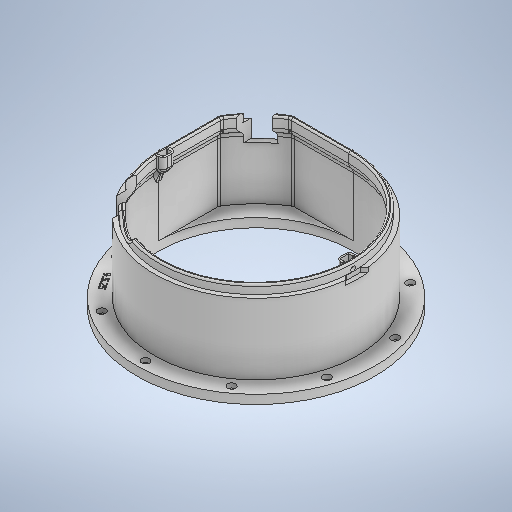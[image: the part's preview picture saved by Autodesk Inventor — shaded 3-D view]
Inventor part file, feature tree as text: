
AUTODESK INVENTOR PART (.ipt)
format: ipt  version: 2025 (Build 290162000, 162)  size: 1,504,256 bytes
history: native  units: mm
features: sketch x15, extrude x10, fillet x5, chamfer x3, hole x2, mirror x2, other x2, pattern_circular x1, plane x1
ambient origin geometry x8: Origin, YZ Plane, XZ Plane, XY Plane, X Axis, Y Axis, Z Axis, Center Point
bodies: Solid1 (feature_tree), Body (feature_tree)
feature tree (41):
  extrude  "Base"  Depth=10.0mm TaperAngle=0.0deg
  extrude  "Walls"  Depth=230.0mm
  extrude  "Overhang for Lip"  Depth=5.0mm TaperAngle=0.0deg
  fillet  "Fillet1"  Radius=5.0mm
  chamfer  "Chamfer1"  Distance=4.99mm Angle=45.0deg
  fillet  "Fillet2"  Radius=8.0mm
  extrude  "Lip"  Depth=5.0mm TaperAngle=0.0deg
  extrude  "8020 Beam Slot"  Depth=30.0mm
  extrude  "LV Window"  Depth=42.0mm
  fillet  "Fillet4"  Radius=53.266mm
  hole  "Hole1"  [1 undecoded]
  pattern_circular  "Circular Pattern1"  Count=10 Angle=360.0deg
  extrude  "Lock Tab Seats"  Depth=5.0mm TaperAngle=0.0deg
  mirror  "Mirror1"
  extrude  "Fill Extra Hole in Base"  Depth=7.0mm
  other  "LABEL"
  other  "DATE"
  plane  "Work Plane2"
  extrude  "Nut & Washer Seat"  Depth=1.0mm TaperAngle=0.0deg
  hole  "Hole2"  [1 undecoded]
  extrude  "Extrusion15"  Depth=5.0mm
  chamfer  "Chamfer2"  Distance=10.0mm
  fillet  "Fillet5"  Radius=17.0mm
  chamfer  "Chamfer3"  Distance=10.0mm
  mirror  "Mirror2"
  fillet  "Fillet7"  Radius=2.0mm
  sketch  "Sketch1"  dims[d1=270.0mm d2=10.0mm d3=0.0mm]
  sketch  "Sketch4"  dims[d15=220.0mm d16=230.0mm]
  sketch  "Sketch7"  dims[d17=80.0mm d18=0.0mm d24=5.0mm d25=0.0mm d26=5.0mm]
  sketch  "Sketch8"  dims[d27=5.0mm d28=4.99mm d29=2.0mm d30=45.0deg d31=8.0mm]
  sketch  "Sketch9"  dims[d32=5.0mm d33=10.0mm d34=0.0mm]
  sketch  "Sketch10"  dims[d36=20.0mm d37=30.0mm]
  sketch  "Sketch11"  dims[d39=0.0mm d40=0.0mm d41=42.0mm d42=53.266mm]
  sketch  "Sketch12"  dims[d43=22.0mm d44=0.0mm d45=0.0mm]
  sketch  "Sketch13"  dims[d46=2.0mm]
  sketch  "Sketch15"  dims[d47=5.5mm d48=6.0mm d49=9.0mm d50=5.0mm d51=90.0deg d52=8.0mm d53=20.594885mm]
  sketch  "Sketch16"  dims[d54=125.0mm d55=100.0mm d56=360.0deg]
  sketch  "Sketch18"  dims[d58=5.0mm d59=0.0mm d60=10.0mm d61=0.0mm]
  sketch  "Sketch19"  dims[d62=8.0mm d63=7.0mm]
  sketch  "Sketch20"  dims[d64=32.0mm d67=1.0mm d68=0.0mm]
  sketch  "Sketch21"  dims[d69=1.0mm d70=0.0mm d71=-118.0mm d76=15.4mm d77=10.0mm d78=17.0mm d79=0.0mm d80=10.0mm d81=2.0mm d82=5.15mm d83=1.6mm d84=5.15mm d85=12.0mm d86=12.7mm d87=0.0mm d88=5.5mm d89=6.0mm d90=4.0mm d91=2.0mm d92=90.0deg d93=8.0mm d94=20.594885mm d95=7.5mm d96=0.8mm d97=0.0mm d98=0.5mm d99=2.0mm d100=45.0deg d101=15.0mm d102=3.5mm d103=2.0mm d104=45.0deg d106=5.0mm d109=88.16mm]
note: 2 required parameter values undecoded (feature->parameter linkage not recoverable at this tier; creation-order binding heuristic only, values carry confidence <= 0.55)
